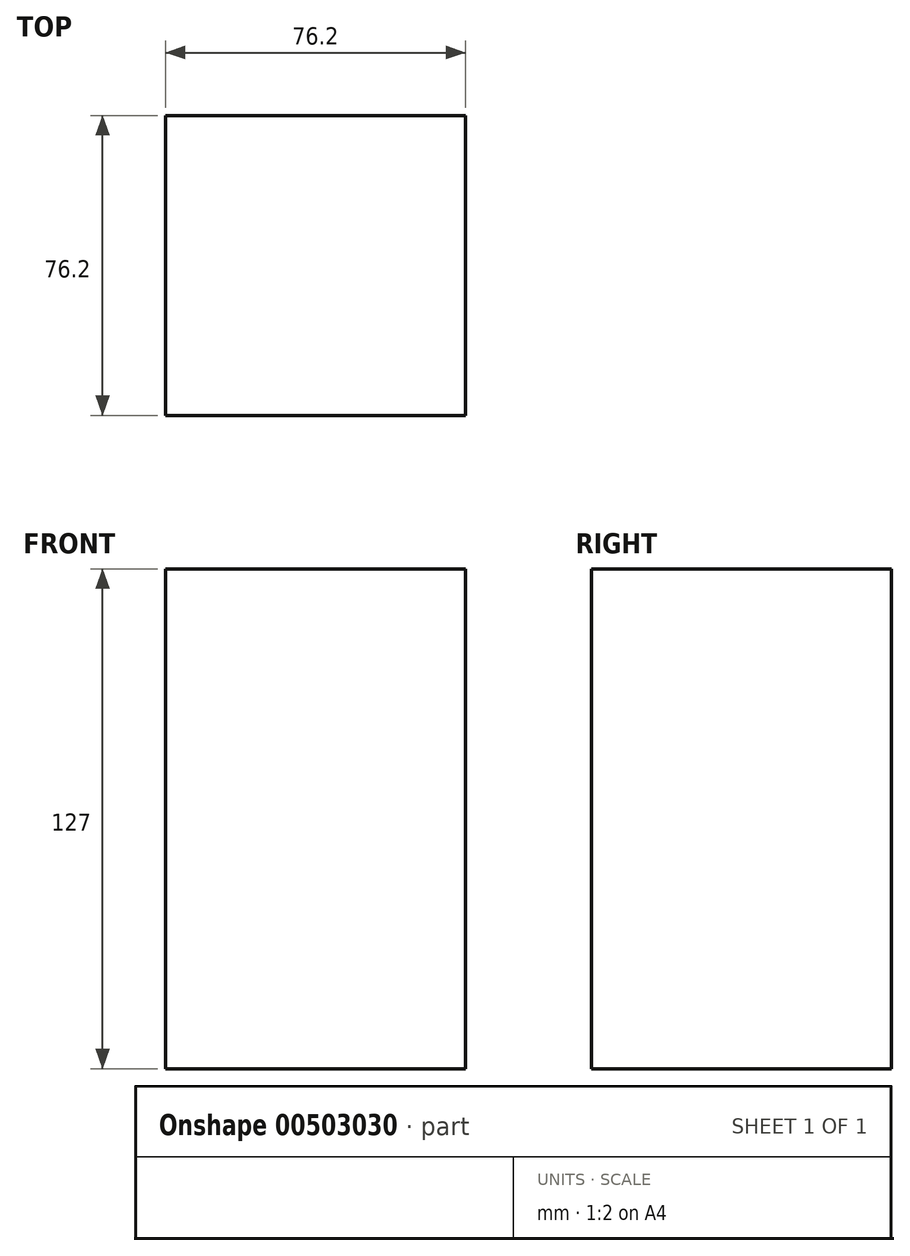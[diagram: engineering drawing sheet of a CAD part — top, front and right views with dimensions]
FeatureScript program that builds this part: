
annotation { "Feature Type Name" : "Feature", "Feature Type Description" : "" }
export const myFeature = defineFeature(function(context is Context, id is Id, definition is map)
    precondition{}
    {
        {
            var Q0;
            Q0=qCreatedBy(makeId("Top.planeOp"),FACE);
            var sketch = newSketch(context, id + "F0", { "sketchPlane" : qUnion([Q0])});
            skLineSegment(sketch, "E0", {"start": v(-38.1, 38.1) * mm, "end": v(38.1, 38.1) * mm});
            skLineSegment(sketch, "E1", {"start": v(38.1, 38.1) * mm, "end": v(38.1, -38.1) * mm});
            skLineSegment(sketch, "E2", {"start": v(-38.1, -38.1) * mm, "end": v(38.1, -38.1) * mm});
            skLineSegment(sketch, "E3", {"start": v(-38.1, -38.1) * mm, "end": v(-38.1, 38.1) * mm});
            skLineSegment(sketch, "E4", {"start": v(0, 0) * mm, "end": v(-38.1, -38.1) * mm, "construction": true});
            skLineSegment(sketch, "E5", {"start": v(0, 0) * mm, "end": v(38.1, -38.1) * mm, "construction": true});
            skLineSegment(sketch, "E6", {"start": v(0, 0) * mm, "end": v(-38.1, 38.1) * mm, "construction": true});
            skSolve(sketch);
        }
        {
            var Q0;
            Q0=makeQuery(id+"F0.imprint","IMPRINT",FACE,{"disambiguationData":[TD([[makeQuery(id+"F0.imprint","IMPRINT",EDGE,{"derivedFrom":sQuery(id+"F0.wireOp",EDGE,"E0")}),-1.0]])]});
            extrude(context, id + "F1", {"entities" : qUnion([Q0]), "depth" : 127 * mm});
        }
    });
